# Revit family: 224_DN125_40-160_RFA_2019
name_source: partatom
category: Pipe Accessories
units: mm (PartAtom-declared; Revit-internal decimal feet)

## family parameters
Always vertical = Yes
Cut with Voids When Loaded = No
Part Type = Valve - Breaks Into
Round Connector Dimension = Use Diameter
Shared = No
Work Plane-Based = No

## types (10) — shared parameters
ANG = 32.00°
ARC1 = 10 mm  [stored 0.0328084 ft]
ARC2 = 2 mm  [stored 0.00656168 ft]
CAT0 = Yes
Description = Regulátor diferenčního tlaku přírubový
L2D = 350 mm
L2D_Min = 3048 mm
Manufacturer = Hydronic Systems Prague s.r.o.
QmdConnectorList = 301;D;302;D
R12 = 43 mm
R4 = 114 mm
R6 = 97 mm
R7 = 36 mm
R8 = 54 mm
Type Comments = přírubový ventil, PN16; -10~+120°C; dpmin=1,5xdpnast;
URL = www.hydronic.cz
W2D = 100 mm
X8 = 31 mm
X9 = 20 mm  [stored 0.0656168 ft]
Y8 = 44 mm
Y9 = 112 mm
magiPartTypeId = 304
magiProductFamilyId = cb96b53648234cefb8c956722b95ac

## per-type parameters (varying)
- 224_DN100_(40-160): A1=52 mm  [stored 0.170604 ft]; A2=32 mm; D=100 mm; D5=65 mm; D6=81 mm; DT2=50 mm  [stored 0.164042 ft]; DT21=50 mm  [stored 0.164042 ft]; FDT2=110 mm; H5=60 mm; L3=63 mm; LT2=175 mm; MC Product Code=224 100 7 (DN100; dpnast 40-160kPa; dpmax=250kPa; kvs=110,0kPa); R10=58 mm; R2=81 mm; R3=52 mm  [stored 0.170604 ft]; R5=110 mm; X1=14 mm  [stored 0.0459318 ft]; X4=91 mm; X5=152 mm; Z1=61 mm; Z2=20 mm  [stored 0.0656168 ft]; Z3=16 mm  [stored 0.0524934 ft]; Z4=41 mm; Z6=102 mm; Z7=8 mm  [stored 0.0262467 ft]; Z8=24 mm; magiProductId=71f9e553003c40d991c5e352e67284
- 224_DN100_(20-70): A1=52 mm  [stored 0.170604 ft]; A2=32 mm; D=100 mm; D5=65 mm; D6=81 mm; DT2=50 mm  [stored 0.164042 ft]; DT21=50 mm  [stored 0.164042 ft]; FDT2=110 mm; H5=60 mm; L3=63 mm; LT2=175 mm; MC Product Code=224 100 3 (DN100; dpnast 20-70kPa; dpmax=250kPa; kvs=110,0kPa); R10=58 mm; R2=81 mm; R3=52 mm  [stored 0.170604 ft]; R5=110 mm; X1=14 mm  [stored 0.0459318 ft]; X4=91 mm; X5=152 mm; Z1=61 mm; Z2=20 mm  [stored 0.0656168 ft]; Z3=16 mm  [stored 0.0524934 ft]; Z4=41 mm; Z6=102 mm; Z7=8 mm  [stored 0.0262467 ft]; Z8=24 mm; magiProductId=5e4de33176c64976a9c157b39996ce
- 224_DN125_(40-160): A1=59 mm; A2=37 mm; D=125 mm; D5=81 mm; D6=102 mm; DT2=63 mm; DT21=63 mm; FDT2=125 mm; H5=63 mm; L3=72 mm; LT2=200 mm; MC Product Code=224 125 7 (DN125; dpnast 40-160kPa; dpmax=250kPa; kvs=169,0kPa); R10=71 mm; R2=96 mm; R3=65 mm; R5=125 mm; X1=16 mm  [stored 0.0524934 ft]; X4=114 mm; X5=166 mm; Z1=65 mm; Z2=22 mm; Z3=17 mm; Z4=43 mm; Z6=108 mm; Z7=9 mm; Z8=26 mm; magiProductId=9beb69b667494b6ab1f54942078ae6
- 224_DN125_(20-70): A1=59 mm; A2=37 mm; D=125 mm; D5=81 mm; D6=102 mm; DT2=63 mm; DT21=63 mm; FDT2=125 mm; H5=63 mm; L3=72 mm; LT2=200 mm; MC Product Code=224 125 3 (DN125; dpnast 20-70kPa; dpmax=250kPa; kvs=169,0kPa); R10=71 mm; R2=96 mm; R3=65 mm; R5=125 mm; X1=16 mm  [stored 0.0524934 ft]; X4=114 mm; X5=166 mm; Z1=65 mm; Z2=22 mm; Z3=17 mm; Z4=43 mm; Z6=108 mm; Z7=9 mm; Z8=26 mm; magiProductId=2c85edc695ca465cb63b6911085491
- 224_DN150_(40-160): A1=71 mm; A2=45 mm; D=150 mm; D5=83 mm; D6=91 mm; DT2=75 mm; DT21=68 mm; FDT2=143 mm; H5=68 mm; L3=87 mm; LT2=240 mm; MC Product Code=224 150 7 (DN150; dpnast 40-160kPa; dpmax=250kPa; kvs=200,0kPa); R10=84 mm; R2=109 mm; R3=70 mm; R5=143 mm; X1=19 mm; X4=116 mm; X5=223 mm; Z1=90 mm; Z2=22 mm; Z3=18 mm; Z4=45 mm; Z6=90 mm; Z7=9 mm; Z8=27 mm; magiProductId=96017eba5eec4de2abe05c4d8dc7d1
- 224_DN150_(20-70): A1=71 mm; A2=45 mm; D=150 mm; D5=83 mm; D6=91 mm; DT2=75 mm; DT21=68 mm; FDT2=143 mm; H5=68 mm; L3=87 mm; LT2=240 mm; MC Product Code=224 150 3 (DN150; dpnast 20-70kPa; dpmax=250kPa; kvs=200,0kPa); R10=84 mm; R2=109 mm; R3=70 mm; R5=143 mm; X1=19 mm; X4=116 mm; X5=223 mm; Z1=90 mm; Z2=22 mm; Z3=18 mm; Z4=45 mm; Z6=90 mm; Z7=9 mm; Z8=27 mm; magiProductId=2dcf3707ec5549d494f72875a03dce
- 224_DN065_(40-160): A1=43 mm; A2=27 mm; D=65 mm; D5=42 mm; D6=53 mm; DT2=33 mm; DT21=33 mm; FDT2=93 mm; H5=60 mm; L3=52 mm  [stored 0.170604 ft]; LT2=145 mm; MC Product Code=224 065 7 (DN65; dpnast 40-160kPa; dpmax=300kPa; kvs=48,4kPa); R10=41 mm; R2=63 mm; R3=34 mm; R5=93 mm; X1=12 mm  [stored 0.0393701 ft]; X4=59 mm; X5=140 mm; Z1=57 mm; Z2=19 mm; Z3=15 mm  [stored 0.0492126 ft]; Z4=38 mm; Z6=96 mm; Z7=8 mm  [stored 0.0262467 ft]; Z8=23 mm; magiProductId=7a3227ed888c4b0d8669ae9eb0085d
- 224_DN065_(20-70): A1=43 mm; A2=27 mm; D=65 mm; D5=42 mm; D6=53 mm; DT2=33 mm; DT21=33 mm; FDT2=93 mm; H5=60 mm; L3=52 mm  [stored 0.170604 ft]; LT2=145 mm; MC Product Code=224 065 3 (DN65; dpnast 20-70kPa; dpmax=300kPa; kvs=48,4kPa); R10=41 mm; R2=63 mm; R3=34 mm; R5=93 mm; X1=12 mm  [stored 0.0393701 ft]; X4=59 mm; X5=140 mm; Z1=57 mm; Z2=19 mm; Z3=15 mm  [stored 0.0492126 ft]; Z4=38 mm; Z6=96 mm; Z7=8 mm  [stored 0.0262467 ft]; Z8=23 mm; magiProductId=bd269db4002540fe9b2a41f205afd7
- 224_DN080_(40-160): A1=46 mm; A2=29 mm; D=80 mm; D5=52 mm  [stored 0.170604 ft]; D6=65 mm; DT2=40 mm  [stored 0.131234 ft]; DT21=40 mm  [stored 0.131234 ft]; FDT2=100 mm; H5=60 mm; L3=55 mm; LT2=155 mm; MC Product Code=224 080 7 (DN80; dpnast 40-160kPa; dpmax=300kPa; kvs=74,5kPa); R10=48 mm  [stored 0.15748 ft]; R2=71 mm; R3=42 mm; R5=100 mm; X1=12 mm  [stored 0.0393701 ft]; X4=73 mm; X5=141 mm; Z1=58 mm; Z2=19 mm; Z3=16 mm  [stored 0.0524934 ft]; Z4=39 mm; Z6=97 mm; Z7=8 mm  [stored 0.0262467 ft]; Z8=23 mm; magiProductId=20b45c03d3cb49e9a44f946d5e2c2d
- 224_DN080_(20-70): A1=46 mm; A2=29 mm; D=80 mm; D5=52 mm  [stored 0.170604 ft]; D6=65 mm; DT2=40 mm  [stored 0.131234 ft]; DT21=40 mm  [stored 0.131234 ft]; FDT2=100 mm; H5=60 mm; L3=55 mm; LT2=155 mm; MC Product Code=224 080 3 (DN80; dpnast 20-70kPa; dpmax=300kPa; kvs=74,5kPa); R10=48 mm  [stored 0.15748 ft]; R2=71 mm; R3=42 mm; R5=100 mm; X1=12 mm  [stored 0.0393701 ft]; X4=73 mm; X5=141 mm; Z1=58 mm; Z2=19 mm; Z3=16 mm  [stored 0.0524934 ft]; Z4=39 mm; Z6=97 mm; Z7=8 mm  [stored 0.0262467 ft]; Z8=23 mm; magiProductId=2f63645f7c5342ecbadd0051fa47f2

note: [stored X ft] marks values corroborated as IEEE doubles in the binary element streams (Revit-internal decimal feet)

## geometry (parser evidence)
native form markers: Sweep x1
no freeform markers — native parametric forms only
